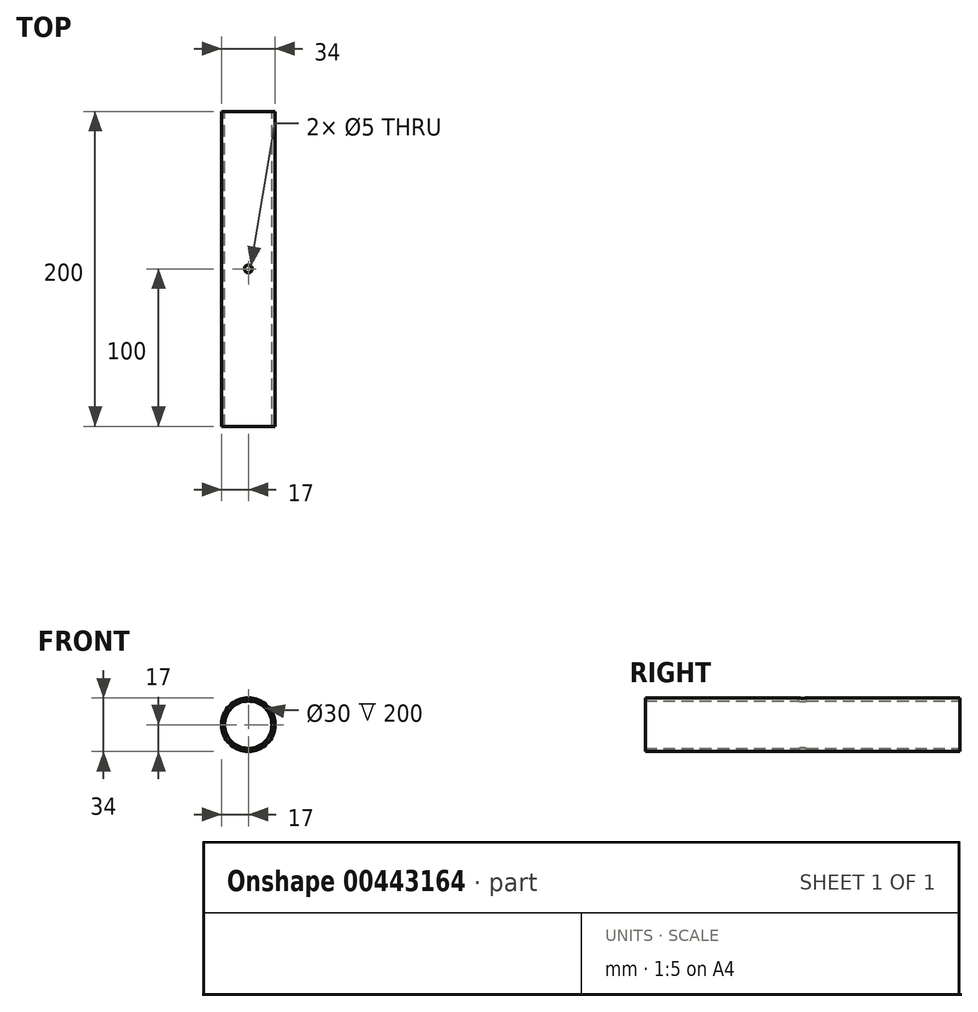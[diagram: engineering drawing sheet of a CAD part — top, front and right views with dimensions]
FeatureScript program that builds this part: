
annotation { "Feature Type Name" : "Feature", "Feature Type Description" : "" }
export const myFeature = defineFeature(function(context is Context, id is Id, definition is map)
    precondition{}
    {
        {
            var Q0;
            Q0=qCreatedBy(makeId("Front.planeOp"),FACE);
            var sketch = newSketch(context, id + "F0", { "sketchPlane" : qUnion([Q0])});
            skCircle(sketch, "E0", {"center": v(0, 0) * mm, "radius": 17 * mm});
            skCircle(sketch, "E1", {"center": v(0, 0) * mm, "radius": 15 * mm});
            skSolve(sketch);
        }
        {
            var Q0;
            Q0=makeQuery(id+"F0.imprint","IMPRINT",FACE,{"disambiguationData":[TD([[makeQuery(id+"F0.imprint","IMPRINT",EDGE,{"derivedFrom":sQuery(id+"F0.wireOp",EDGE,"E0")}),1.0]])]});
            extrude(context, id + "F1", {"entities" : qUnion([Q0]), "depth" : 200 * mm});
        }
        {
            var Q0;
            Q0=qCreatedBy(makeId("Top.planeOp"),FACE);
            var sketch = newSketch(context, id + "F2", { "sketchPlane" : qUnion([Q0])});
            skCircle(sketch, "E2", {"center": v(0, -100) * mm, "radius": 2.5 * mm});
            skLineSegment(sketch, "E3", {"start": v(0, 0) * mm, "end": v(0, -84.8) * mm, "construction": true});
            skLineSegment(sketch, "E4", {"start": v(0, -84.8) * mm, "end": v(-17, -84.8) * mm, "construction": true});
            skSolve(sketch);
        }
        {
            var Q0;
            Q0 = qSketchRegion(id + "F2", true);
            extrude(context, id + "F3", {"entities" : qUnion([Q0]), "operationType" : NewBodyOperationType.REMOVE, "oppositeDirection" : true, "depth" : 25 * mm, "hasSecondDirection" : true, "secondDirectionOppositeDirection" : false, "secondDirectionDepth" : 25 * mm});
        }
    });
